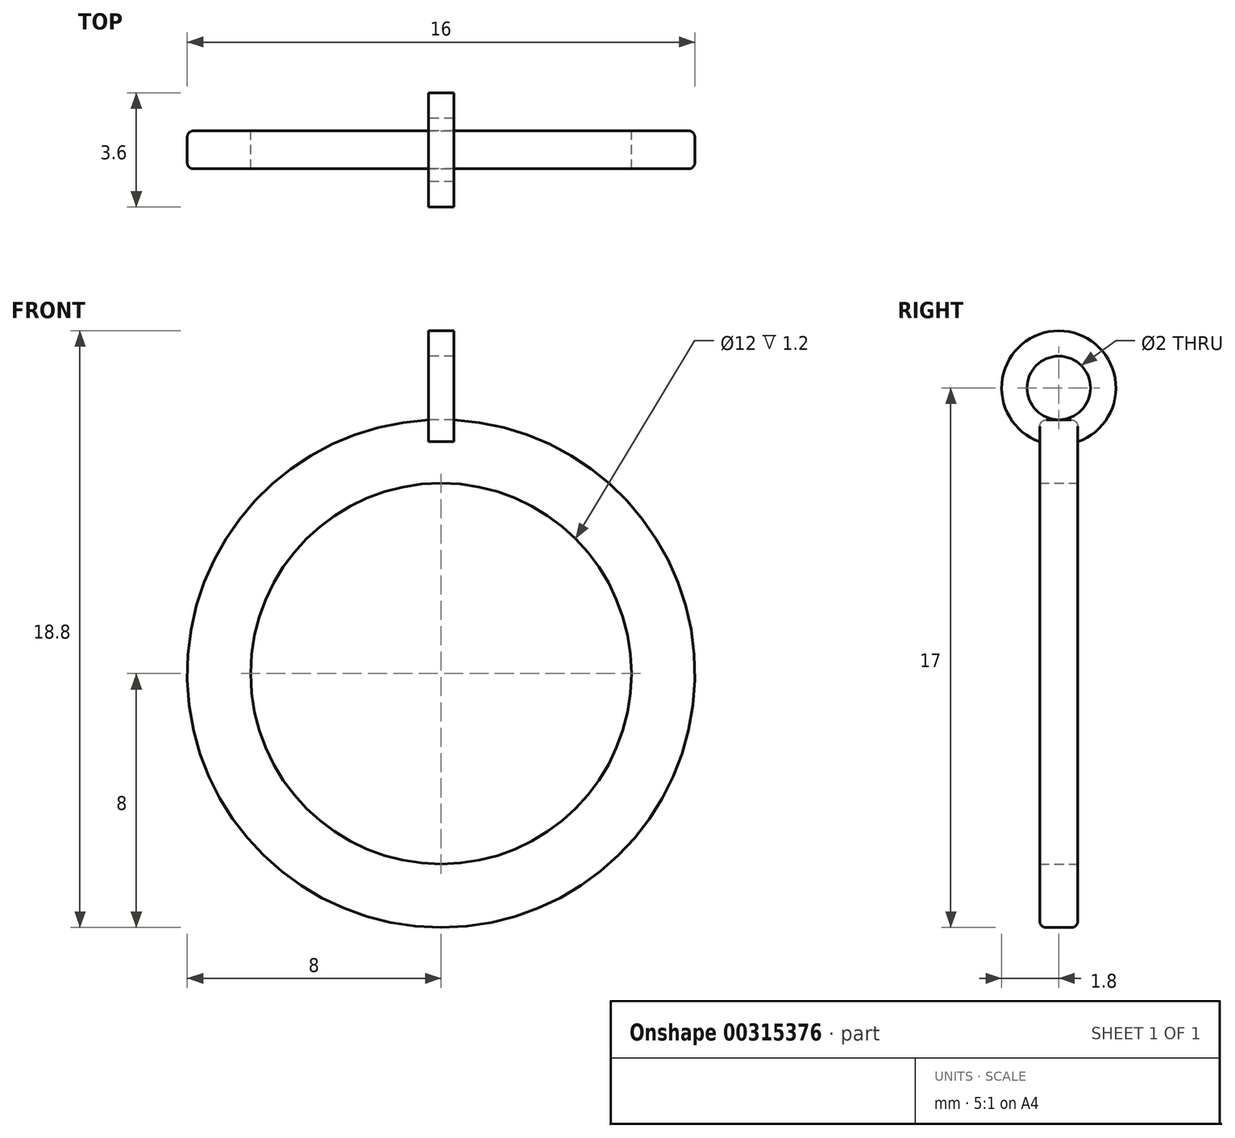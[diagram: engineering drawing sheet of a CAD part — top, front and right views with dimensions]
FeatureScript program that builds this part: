
annotation { "Feature Type Name" : "Feature", "Feature Type Description" : "" }
export const myFeature = defineFeature(function(context is Context, id is Id, definition is map)
    precondition{}
    {
        {
            var Q0;
            Q0=qCreatedBy(makeId("Front.planeOp"),FACE);
            var sketch = newSketch(context, id + "F0", { "sketchPlane" : qUnion([Q0])});
            skCircle(sketch, "E0", {"center": v(0, 0) * mm, "radius": 8 * mm});
            skCircle(sketch, "E1", {"center": v(0, 0) * mm, "radius": 6 * mm});
            skSolve(sketch);
        }
        {
            var Q0;
            Q0 = qSketchRegion(id + "F0", true);
            extrude(context, id + "F1", {"entities" : qUnion([Q0]), "endBound" : BoundingType.SYMMETRIC, "depth" : 1.2 * mm});
        }
        {
            var Q0;
            Q0=qCreatedBy(makeId("Right.planeOp"),FACE);
            var sketch = newSketch(context, id + "F2", { "sketchPlane" : qUnion([Q0])});
            skCircle(sketch, "E2", {"center": v(0, 9) * mm, "radius": 1.8 * mm});
            skCircle(sketch, "E3", {"center": v(0, 9) * mm, "radius": 1 * mm});
            skSolve(sketch);
        }
        {
            var Q0;
            Q0=makeQuery(id+"F2.imprint","IMPRINT",FACE,{"disambiguationData":[TD([[makeQuery(id+"F2.imprint","IMPRINT",EDGE,{"derivedFrom":sQuery(id+"F2.wireOp",EDGE,"E2")}),1.0]])]});
            extrude(context, id + "F3", {"entities" : qUnion([Q0]), "operationType" : NewBodyOperationType.ADD, "endBound" : BoundingType.SYMMETRIC, "depth" : 0.8 * mm});
        }
        {
            var Q0;
            Q0=makeQuery(id+"F1.opExtrude","CAP_EDGE",EDGE,{"disambiguationData":[OSD([sQuery(id+"F0.wireOp",EDGE,"E0")])],"isStart":false});
            var Q1;
            Q1=makeQuery(id+"F1.opExtrude","CAP_EDGE",EDGE,{"disambiguationData":[OSD([sQuery(id+"F0.wireOp",EDGE,"E0")])],"isStart":true});
            fillet(context, id + "F4", {"entities" : qUnion([Q0, Q1]), "radius" : 0.2 * mm, "tangentPropagation" : true, "allowEdgeOverflow" : false});
        }
    });
